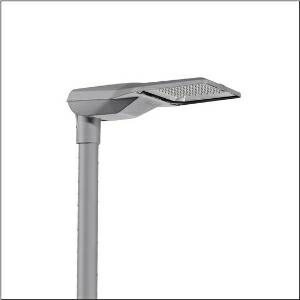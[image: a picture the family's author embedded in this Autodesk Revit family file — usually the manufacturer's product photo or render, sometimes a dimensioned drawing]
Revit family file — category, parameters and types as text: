
# Revit family: streetlight_sl_21_iq_midi___p0_8a_5xe3u31d08mb_ad50
name_source: partatom
category: Lighting Fixtures
units: mm (PartAtom-declared; Revit-internal decimal feet)

## family parameters
Cut with Voids When Loaded = No
Host = Face
Light Source = No
Part Type = Normal
Room Calculation Point = No
Round Connector Dimension = Use Diameter
Shared = No

## types (1)
- --- (1 x LED, 19670 lm, 146.7 W, 3000K)
    Apparent Load = 147 VA
    CIE Flux Codes = 33 69 96 100 100
    Color Rendering = 70
    Color Temperature = 3000K
    Default Elevation = 1800 mm
    Description = Streetlight SL 21 iQ midi, mast luminaire, primary light control with lens, of PMMA, primary optical cover: cover, of toughened safety glass, transparent, light distribution: P0.8a, light emission: direct distribution, primary light characteristic: asymmetric, installation type: post-top, side-entry, LED, High Power LED, rated luminous flux: 19.670lm, luminous efficacy: 134lm/W, light colour: 730, colour temperature: 3000K, control gear: iQ-Comfort, control: pre-setting: linear dimming characteristic, Auto-Match, Temp-Guard, Lumen-Switch, Night-Set, Smart-Wire, Light-Fading, Desk-Remote (wireless, voltage-free reading and setting of iQ features in the workshop via application-optimized NFC function/RFID function), optimised constant luminous flux control (CLO 2.0), mains connection: 230..240V, AC, 50/60Hz, start of lifetime: 147W, end of service life: 161W, reduction: 62W, luminaire housing, of diecast aluminium, powder-coated, Siteco® metallic grey (DB 702S), corrosivity category C5 mid according to DIN EN ISO 12944, please order mast flange separately, inclination adjustable: 0°, 5°, 10°, 15°, sealing non-destructively replaceable, multi-level sealing system, length: 644mm, width: 335mm, height: 110mm, mast flange for spigot size: 42mm (side-entry): 5XC10008XM4, 60/48mm (side-entry/post-top): 5XC10108XM2, 76/60mm (side-entry/post-top): 5XC10108XM1, mounting height: 4..8m, protection rating (complete): IP66, insulation class (complete): insulation class II (safety insulation), certification: CE, ENEC, ENEC+, VDE, impact resistance: IK10, permissible operating ambient temperature for outdoor applications: -40..+50°C, standard-compliant lighting for roads and squares, packaging unit: 1 piece

Light Distribution: P0.8a
    Height = 111 mm
    Lamp = 1 x LED
    Lamp Light Flux = 19670 lm
    Lamp Power = 146.7 W
    Lamp count = 1
    Length = 644 mm
    Luminous efficacy = 134 lm/W
    Manufacturer = Siteco
    ModVariant = No
    Model = 5XE3U31D08MB
    Number of Poles = 1
    OnlyDefault = Yes
    Power Factor = 1
    Product Name = Streetlight SL 21 iQ midi | P0.8a
    Product group = mast luminaire | pylon top
    ProductGroupID = 6100
    Protection Class = Protection class II
    Protection Degree = IP 66
    RLX_Detail_Level = 1
    RLX_Emergency_Light_Flux = 0 lm
    RLX_Emergency_Type = 0
    RLX_Emergency_Type_DB = No
    RlxData = <blob elided: 26761 chars, md5=a0f76684>
    Socket = socket
    Standby Power = 0 W
    System Light Flux = 19670 lm
    System Power = 147 W
    Type Comments = factory setting: luminous flux: 100 % | dim-lin: 254 | 753 mA
    Type Image = l_1004298.jpg
    URL = http://relux.com
    VarID = @adj_072364
    Voltage = 0 V
    Weight = 0.00 kg
    Width = 336 mm

## geometry (parser evidence)
native form markers: Blend x4, Sweep x12
no freeform markers — native parametric forms only
